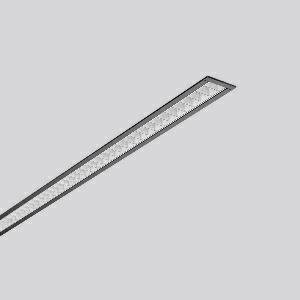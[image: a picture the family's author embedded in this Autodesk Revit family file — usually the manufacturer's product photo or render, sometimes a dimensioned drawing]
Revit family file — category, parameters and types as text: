
# Revit family: less_is_more_27_312177_003_1_76_cbb8
name_source: partatom
category: Lighting Fixtures
units: mm (PartAtom-declared; Revit-internal decimal feet)

## family parameters
Cut with Voids When Loaded = No
Host = Face
Light Source = No
Part Type = Normal
Room Calculation Point = No
Round Connector Dimension = Use Diameter
Shared = No

## types (1)
- LESS IS MORE 27 (1 x LED Modul 840, 2350 lm, 4000)
    Apparent Load = 25 VA
    CIE Flux Codes = 90 99 100 100 100
    Color Rendering = 80
    Color Temperature = 4000
    Default Elevation = 1800 mm
    Description = Series: LESS IS MORE 27
Recessed ceiling and wall luminaire with slim design. Housing: extruded aluminium profile, powder-coated. End cap aluminium powder-coated. High polish aluminium micro grid. Perfect for office areas (RUG < 19) and environments with computer screens in accordance with EN 12464-1. Suitable for Recessed ceiling mounting, wall (recessed). External driver with connecting cable. 
Colour: deep black, matt (RAL 9005)
Length: 1014 mm
Width: 38 mm
Height: 2 mm
Cut-out length: 1006 mm
Cut-out width: 30 mm
Recess height: 45-60 mm
Luminaire: recess height: 37 mm
Lamp: LED
Socket: without socket
Colour temperature: 4000K
Colour rendering index (CRI): 82
System power: 25 W
Rated luminous flux: 2350 lm
Luminous efficiency: 94 lm/W
Control gear: Voltage converter, DALI dim.
Protection class: II
Type of protection: IP 20
    Height = 0 mm  [stored 0 ft]
    Lamp = 1 x LED Modul 840
    Lamp Light Flux = 2350 lm
    Lamp count = 1
    Length = 1014 mm
    Lifetime = 50000 h
    Luminous efficacy = 94 lm/W
    Manufacturer = RZB
    ModVariant = No
    Model = 312177.003.1.76
    Mounting Place = Ceiling, Wall
    Mounting Type = Recessed
    Number of Poles = 1
    OnlyDefault = Yes
    Power Factor = 1
    Product Name = LESS IS MORE 27
    Product group = Recessed LED linear luminaires
    ProductGroupID = 407
    Protection Class = Protection class II
    Protection Degree = IP 20
    RLX_Detail_Level = 1
    RLX_Emergency_Light_Flux = 0 lm
    RLX_Emergency_Type = 0
    RLX_Emergency_Type_DB = No
    RlxData = <blob elided: 29877 chars, md5=df7afe94>
    Socket = socket
    Standby Power = 0 W
    System Light Flux = 2350 lm
    System Power = 25 W
    Type Comments = Product without accessories
    Type Image = 312177.003.jpg
    URL = http://relux.com
    VarID = ---
    Voltage = 230 V
    Voltage Range = 220-240 V
    Weight = 0.00 kg
    Width = 38 mm

note: [stored X ft] marks values corroborated as IEEE doubles in the binary element streams (Revit-internal decimal feet)

## geometry (parser evidence)
native form markers: Blend x4, Sweep x8
no freeform markers — native parametric forms only
